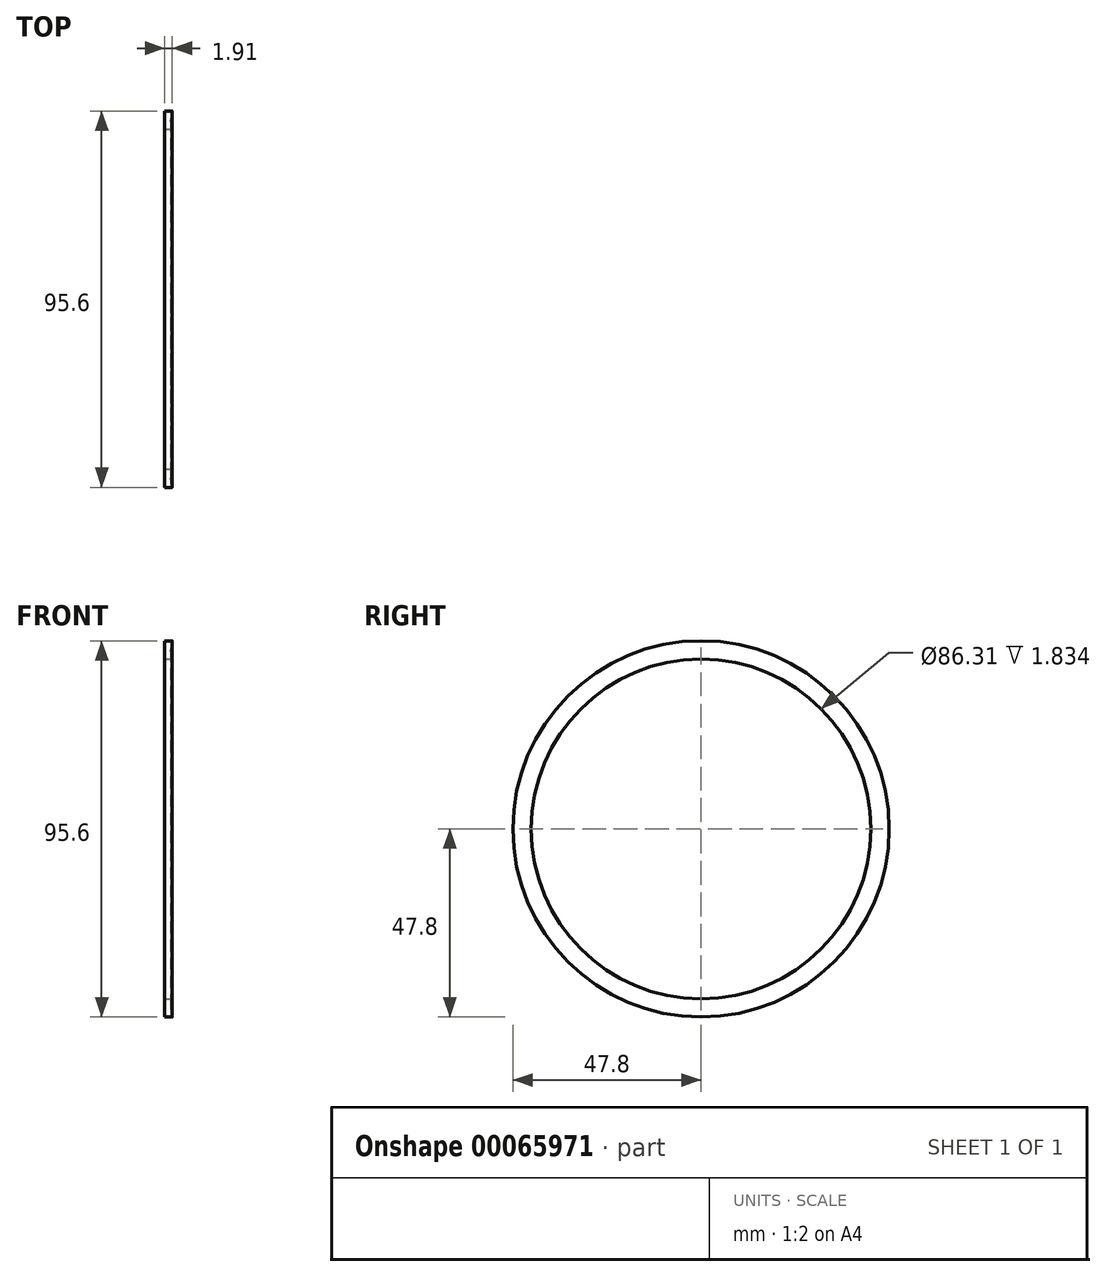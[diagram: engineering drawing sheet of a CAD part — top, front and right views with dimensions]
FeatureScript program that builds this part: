
annotation { "Feature Type Name" : "Feature", "Feature Type Description" : "" }
export const myFeature = defineFeature(function(context is Context, id is Id, definition is map)
    precondition{}
    {
        {
            var Q0;
            Q0=qCreatedBy(makeId("Front.planeOp"),FACE);
            var sketch = newSketch(context, id + "F0", { "sketchPlane" : qUnion([Q0])});
            skLineSegment(sketch, "E0.bottom", {"start": v(-0.1, 47.8) * mm, "end": v(-1.94, 47.8) * mm});
            skLineSegment(sketch, "E0.top", {"start": v(-0.1, 43.15) * mm, "end": v(-1.94, 43.15) * mm});
            skLineSegment(sketch, "E0.right", {"start": v(-1.94, 47.8) * mm, "end": v(-1.94, 43.15) * mm});
            skLineSegment(sketch, "E1", {"start": v(0, 0) * mm, "end": v(-6.16, 0) * mm, "construction": true});
            skArc(sketch, "E2", {"start": v(-0.04, 47.7) * mm, "mid": v(-0.42, 45.48) * mm, "end": v(-0.04, 43.26) * mm});
            skPoint(sketch, "E3.visualSharp", {"position": v(0, 47.8) * mm});
            skArc(sketch, "E3.filletArc", {"start": v(-0.04, 47.7) * mm, "mid": v(-0.05, 47.77) * mm, "end": v(-0.1, 47.8) * mm});
            skPoint(sketch, "E4.visualSharp", {"position": v(0, 43.15) * mm});
            skArc(sketch, "E4.filletArc", {"start": v(-0.1, 43.15) * mm, "mid": v(-0.05, 43.19) * mm, "end": v(-0.04, 43.26) * mm});
            skLineSegment(sketch, "E5", {"start": v(0, 43.15) * mm, "end": v(0, 0) * mm, "construction": true});
            skSolve(sketch);
        }
        {
            var Q0;
            Q0=makeQuery(id+"F0.imprint","IMPRINT",FACE,{"disambiguationData":[TD([[makeQuery(id+"F0.imprint","IMPRINT",EDGE,{"derivedFrom":sQuery(id+"F0.wireOp",EDGE,"E0.bottom")}),1.0]])]});
            var Q1;
            Q1=sQuery(id+"F0.wireOp",EDGE,"E1");
            revolve(context, id + "F1", {"entities" : qUnion([Q0]), "axis" : qUnion([Q1]), "revolveType" : RevolveType.FULL});
        }
    });
